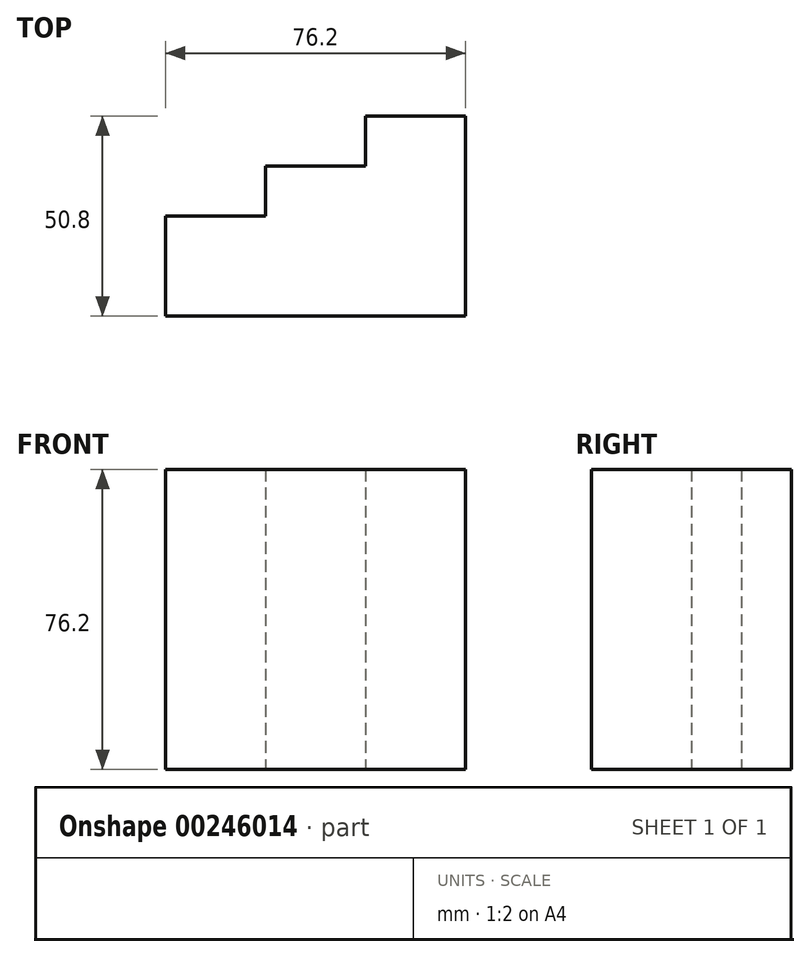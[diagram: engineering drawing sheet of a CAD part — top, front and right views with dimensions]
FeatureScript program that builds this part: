
annotation { "Feature Type Name" : "Feature", "Feature Type Description" : "" }
export const myFeature = defineFeature(function(context is Context, id is Id, definition is map)
    precondition{}
    {
        {
            var Q0;
            Q0=qCreatedBy(makeId("Top.planeOp"),FACE);
            var sketch = newSketch(context, id + "F0", { "sketchPlane" : qUnion([Q0])});
            skLineSegment(sketch, "E0", {"start": v(0, 0) * mm, "end": v(-38.1, 0) * mm});
            skLineSegment(sketch, "E1", {"start": v(0, 0) * mm, "end": v(38.1, 0) * mm});
            skLineSegment(sketch, "E2", {"start": v(-38.1, 0) * mm, "end": v(-38.1, 25.4) * mm});
            skLineSegment(sketch, "E3", {"start": v(-38.1, 25.4) * mm, "end": v(-12.7, 25.4) * mm});
            skLineSegment(sketch, "E4", {"start": v(-12.7, 25.4) * mm, "end": v(-12.7, 38.1) * mm});
            skLineSegment(sketch, "E5", {"start": v(-12.7, 38.1) * mm, "end": v(12.7, 38.1) * mm});
            skLineSegment(sketch, "E6", {"start": v(12.7, 38.1) * mm, "end": v(12.7, 50.8) * mm});
            skLineSegment(sketch, "E7", {"start": v(12.7, 50.8) * mm, "end": v(38.1, 50.8) * mm});
            skLineSegment(sketch, "E8", {"start": v(38.1, 50.8) * mm, "end": v(38.1, 0) * mm});
            skSolve(sketch);
        }
        {
            var Q0;
            Q0=makeQuery(id+"F0.imprint","IMPRINT",FACE,{"disambiguationData":[TD([[makeQuery(id+"F0.imprint","IMPRINT",EDGE,{"derivedFrom":sQuery(id+"F0.wireOp",EDGE,"E0")}),-1.0]])]});
            extrude(context, id + "F1", {"entities" : qUnion([Q0]), "depth" : 76.2 * mm});
        }
    });
